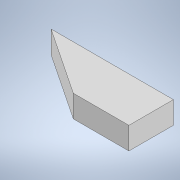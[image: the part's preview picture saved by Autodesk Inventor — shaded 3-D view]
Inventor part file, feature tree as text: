
AUTODESK INVENTOR PART (.ipt)
format: ipt  version: 2021 (Build 250183000, 183)  size: 100,864 bytes
history: native  units: mm
features: extrude x2, sketch x2, other x1
ambient origin geometry x8: Origin, YZ Plane, XZ Plane, XY Plane, X Axis, Y Axis, Z Axis, Center Point
bodies: Body1 (feature_tree)
feature tree (5):
  other  "ソリッド1"
  extrude  "押し出し1"  Depth=2000.0mm TaperAngle=0.0deg
  extrude  "押し出し5"  Depth=5500.0mm
  sketch  "スケッチ1"
  sketch  "スケッチ5"
